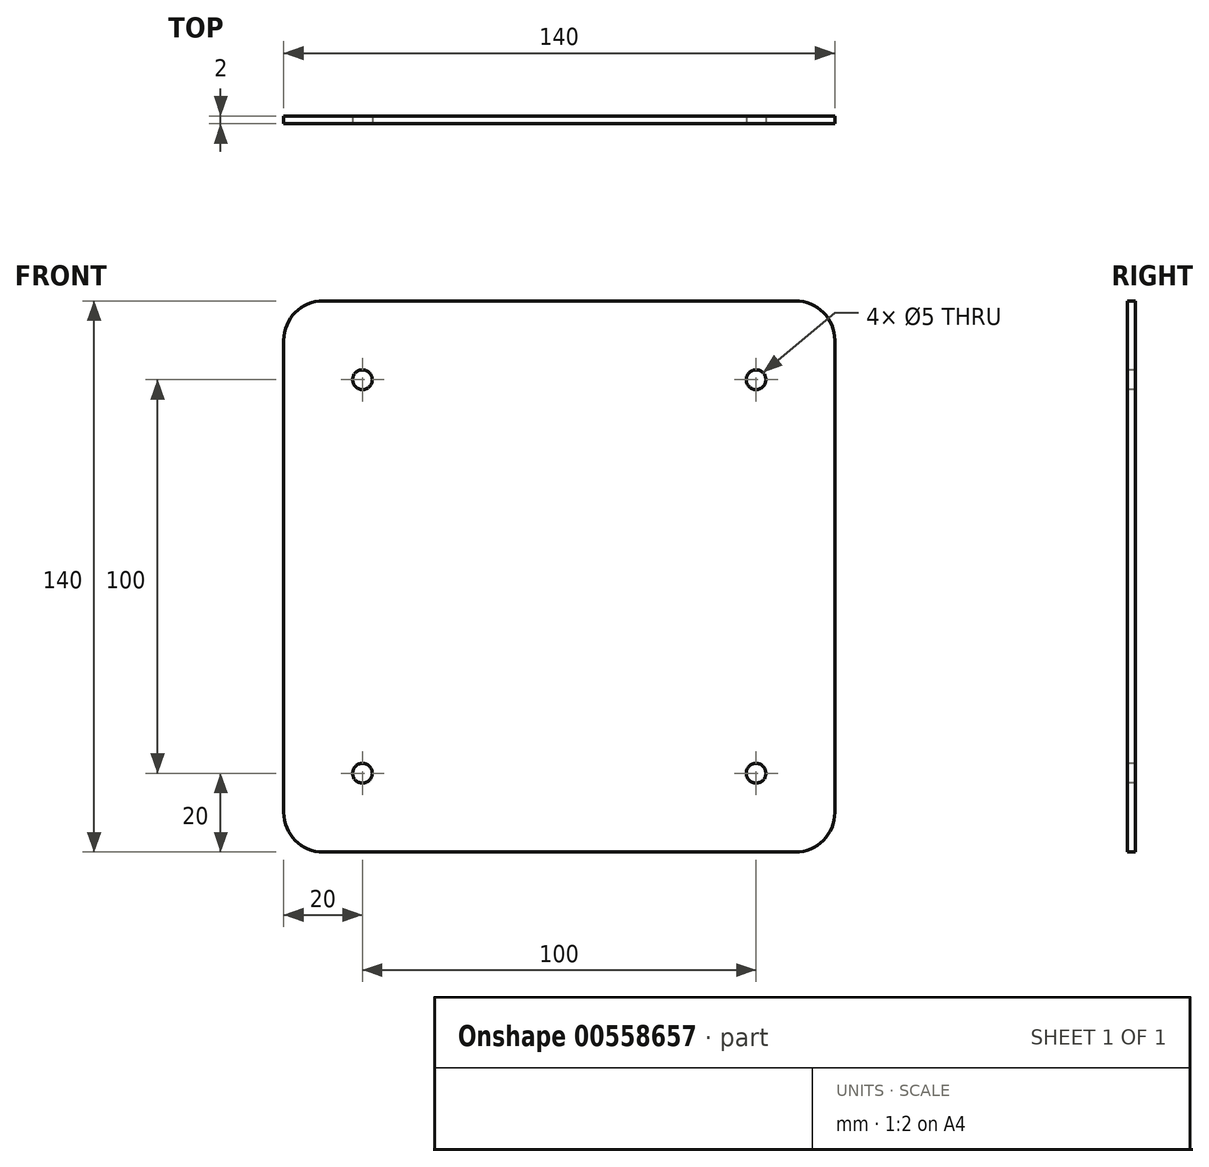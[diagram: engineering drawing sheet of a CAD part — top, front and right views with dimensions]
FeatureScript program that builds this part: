
annotation { "Feature Type Name" : "Feature", "Feature Type Description" : "" }
export const myFeature = defineFeature(function(context is Context, id is Id, definition is map)
    precondition{}
    {
        {
            var Q0;
            Q0=qCreatedBy(makeId("Front.planeOp"),FACE);
            var sketch = newSketch(context, id + "F0", { "sketchPlane" : qUnion([Q0])});
            skLineSegment(sketch, "E0.bottom", {"start": v(-70, -70) * mm, "end": v(70, -70) * mm});
            skLineSegment(sketch, "E0.top", {"start": v(-70, 70) * mm, "end": v(70, 70) * mm});
            skLineSegment(sketch, "E0.left", {"start": v(-70, -70) * mm, "end": v(-70, 70) * mm});
            skLineSegment(sketch, "E0.right", {"start": v(70, -70) * mm, "end": v(70, 70) * mm});
            skPoint(sketch, "E0.middle", {"position": v(0, 0) * mm});
            skSolve(sketch);
        }
        {
            var Q0;
            Q0=makeQuery(id+"F0.imprint","IMPRINT",FACE,{"disambiguationData":[TD([[makeQuery(id+"F0.imprint","IMPRINT",EDGE,{"derivedFrom":sQuery(id+"F0.wireOp",EDGE,"E0.bottom")}),1.0]])]});
            extrude(context, id + "F1", {"entities" : qUnion([Q0]), "depth" : 2 * mm, "offsetDistance" : 25 * mm});
        }
        {
            var Q0;
            Q0=makeQuery(id+"F1.opExtrude","CAP_FACE",FACE,{"disambiguationData":[OSD([sQuery(id+"F0.wireOp",EDGE,"E0.bottom"),sQuery(id+"F0.wireOp",EDGE,"E0.top"),sQuery(id+"F0.wireOp",EDGE,"E0.left"),sQuery(id+"F0.wireOp",EDGE,"E0.right")])],"isStart":false});
            var sketch = newSketch(context, id + "F2", { "sketchPlane" : qUnion([Q0])});
            skPoint(sketch, "E1.middle", {"position": v(0, 0) * mm});
            skCircle(sketch, "E2", {"center": v(-50, 50) * mm, "radius": 2.5 * mm});
            skCircle(sketch, "E3", {"center": v(50, 50) * mm, "radius": 2.5 * mm});
            skCircle(sketch, "E4", {"center": v(-50, -50) * mm, "radius": 2.5 * mm});
            skCircle(sketch, "E5", {"center": v(50, -50) * mm, "radius": 2.5 * mm});
            skSolve(sketch);
        }
        {
            var Q0;
            Q0 = qSketchRegion(id + "F2", true);
            extrude(context, id + "F3", {"entities" : qUnion([Q0]), "operationType" : NewBodyOperationType.REMOVE, "oppositeDirection" : true, "depth" : 25 * mm, "offsetDistance" : 25 * mm});
        }
        {
            var Q0;
            Q0=makeQuery(id+"F1.opExtrude","SWEPT_EDGE",EDGE,{"disambiguationData":[OSD([sQuery(id+"F0.wireOp",EDGE,"E0.top"),sQuery(id+"F0.wireOp",EDGE,"E0.right")])]});
            var Q1;
            Q1=makeQuery(id+"F1.opExtrude","SWEPT_EDGE",EDGE,{"disambiguationData":[OSD([sQuery(id+"F0.wireOp",EDGE,"E0.bottom"),sQuery(id+"F0.wireOp",EDGE,"E0.right")])]});
            var Q2;
            Q2=makeQuery(id+"F1.opExtrude","SWEPT_EDGE",EDGE,{"disambiguationData":[OSD([sQuery(id+"F0.wireOp",EDGE,"E0.top"),sQuery(id+"F0.wireOp",EDGE,"E0.left")])]});
            var Q3;
            Q3=makeQuery(id+"F1.opExtrude","SWEPT_EDGE",EDGE,{"disambiguationData":[OSD([sQuery(id+"F0.wireOp",EDGE,"E0.bottom"),sQuery(id+"F0.wireOp",EDGE,"E0.left")])]});
            fillet(context, id + "F4", {"entities" : qUnion([Q0, Q1, Q2, Q3]), "radius" : 10 * mm, "tangentPropagation" : true, "allowEdgeOverflow" : false});
        }
    });
